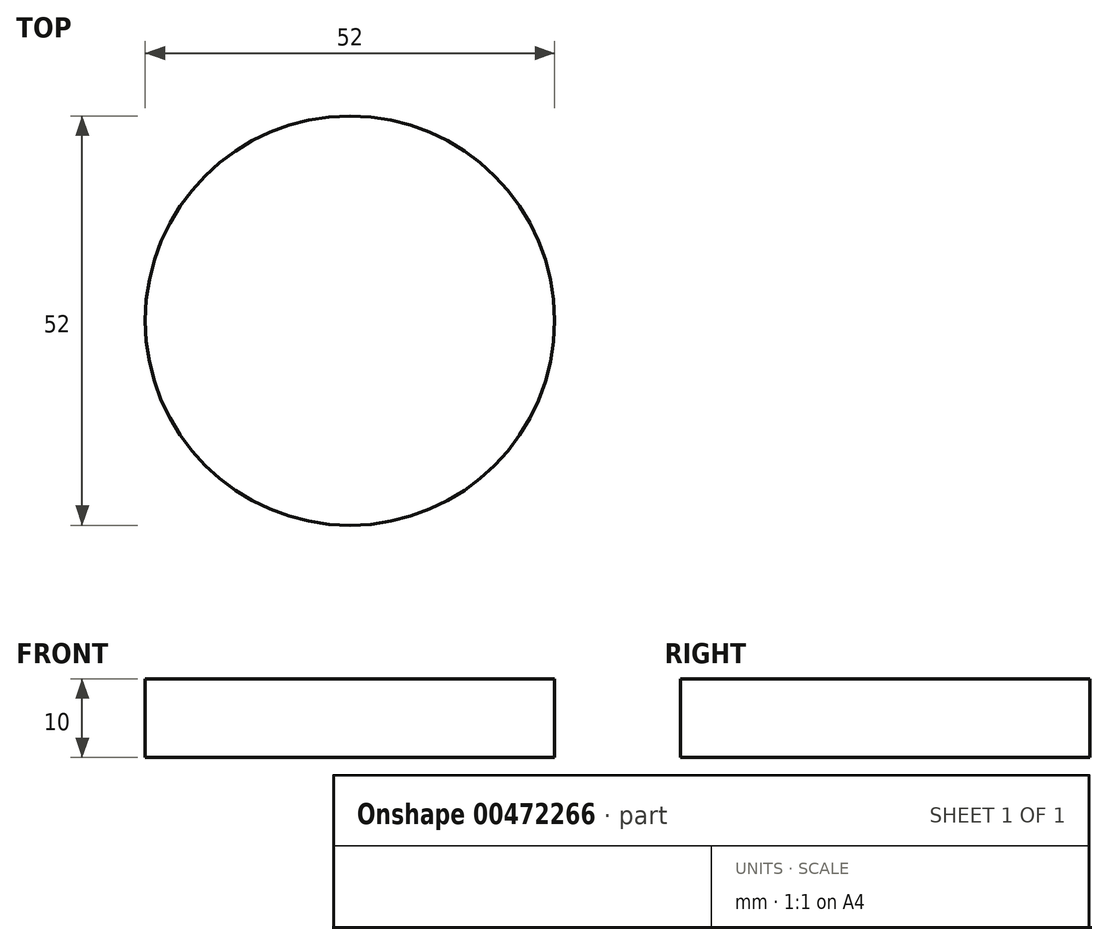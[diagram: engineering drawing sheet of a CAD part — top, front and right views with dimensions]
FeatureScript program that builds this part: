
annotation { "Feature Type Name" : "Feature", "Feature Type Description" : "" }
export const myFeature = defineFeature(function(context is Context, id is Id, definition is map)
    precondition{}
    {
        {
            var Q0;
            Q0=qCreatedBy(makeId("Top.planeOp"),FACE);
            var sketch = newSketch(context, id + "F0", { "sketchPlane" : qUnion([Q0])});
            skCircle(sketch, "E0", {"center": v(-46.3, 17.12) * mm, "radius": 25.5 * mm});
            skCircle(sketch, "E1", {"center": v(-46.3, 17.12) * mm, "radius": 26 * mm});
            skSolve(sketch);
        }
        {
            var Q0;
            Q0=sQuery(id+"F0.wireOp",EDGE,"E1");
            var Q1;
            Q1=sQuery(id+"F0.wireOp",EDGE,"E0");
            extrude(context, id + "F1", {"bodyType" : ToolBodyType.SURFACE, "surfaceEntities" : qUnion([Q0, Q1]), "depth" : 50 * mm});
        }
        {
            var Q0;
            Q0=qCreatedBy(makeId("Top.planeOp"),FACE);
            var sketch = newSketch(context, id + "F2", { "sketchPlane" : qUnion([Q0])});
            skCircle(sketch, "E2", {"center": v(-46.3, 17.12) * mm, "radius": 26 * mm});
            skSolve(sketch);
        }
        {
            var Q0;
            Q0 = qSketchRegion(id + "F2", true);
            extrude(context, id + "F3", {"entities" : qUnion([Q0]), "depth" : 10 * mm});
        }
    });
